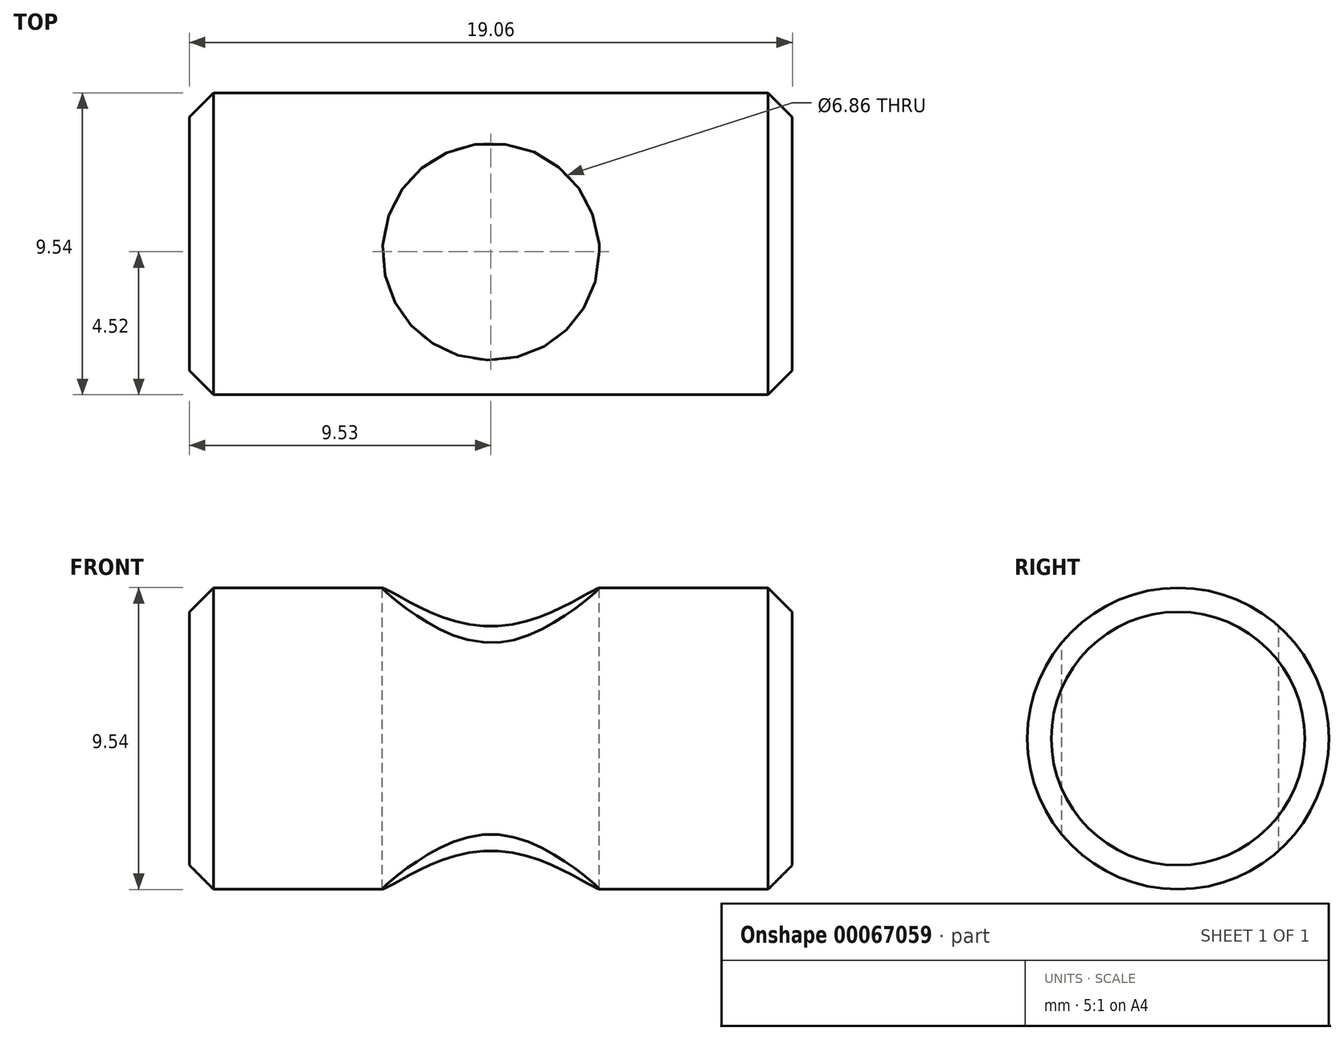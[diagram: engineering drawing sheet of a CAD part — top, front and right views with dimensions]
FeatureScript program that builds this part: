
annotation { "Feature Type Name" : "Feature", "Feature Type Description" : "" }
export const myFeature = defineFeature(function(context is Context, id is Id, definition is map)
    precondition{}
    {
        {
            var Q0;
            Q0=qCreatedBy(makeId("Right.planeOp"),FACE);
            var sketch = newSketch(context, id + "F0", { "sketchPlane" : qUnion([Q0])});
            skCircle(sketch, "E0", {"center": v(0, 0) * mm, "radius": 4.77 * mm});
            skSolve(sketch);
        }
        {
            var Q0;
            Q0=qSketchRegion(id+"F0",true);
            extrude(context, id + "F1", {"entities" : qUnion([Q0]), "endBound" : BoundingType.SYMMETRIC, "depth" : 19.05 * mm});
        }
        {
            var Q0;
            Q0=makeQuery(id+"F1.opExtrude","SWEPT_FACE",FACE,{"disambiguationData":[OSD([sQuery(id+"F0.wireOp",EDGE,"E0")])]});
            chamfer(context, id + "F2", {"entities" : qUnion([Q0]), "width" : 0.76 * mm, "tangentPropagation" : true});
        }
        {
            var Q0;
            Q0=qCreatedBy(makeId("Top.planeOp"),FACE);
            var sketch = newSketch(context, id + "F3", { "sketchPlane" : qUnion([Q0])});
            skCircle(sketch, "E1", {"center": v(0, -0.25) * mm, "radius": 3.43 * mm});
            skSolve(sketch);
        }
        {
            var Q0;
            Q0=qSketchRegion(id+"F3",true);
            extrude(context, id + "F4", {"entities" : qUnion([Q0]), "operationType" : NewBodyOperationType.REMOVE, "endBound" : BoundingType.SYMMETRIC, "oppositeDirection" : true, "depth" : 25.4 * mm});
        }
    });
